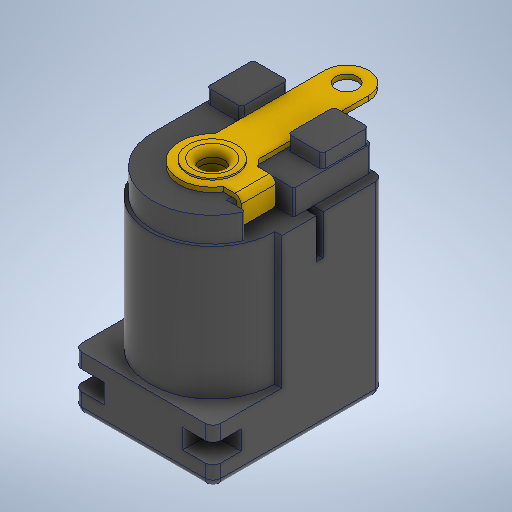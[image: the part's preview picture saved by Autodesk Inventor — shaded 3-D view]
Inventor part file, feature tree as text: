
AUTODESK INVENTOR PART (.ipt)
format: ipt  version: 2025 (Build 290162000, 162)  size: 686,080 bytes
history: native  units: in
note: dims shown in document units (in); Inventor stores cm internally (conversion verified against a paired STEP export)
features: fillet x1
ambient origin geometry x8: Origin, YZ Plane, XZ Plane, XY Plane, X Axis, Y Axis, Z Axis, Center Point
bodies: Solid1 (feature_tree)
feature tree (1):
  fillet  "Fillet1"  [1 undecoded]
note: 1 required parameter value undecoded (feature->parameter linkage not recoverable at this tier; creation-order binding heuristic only, values carry confidence <= 0.55)
